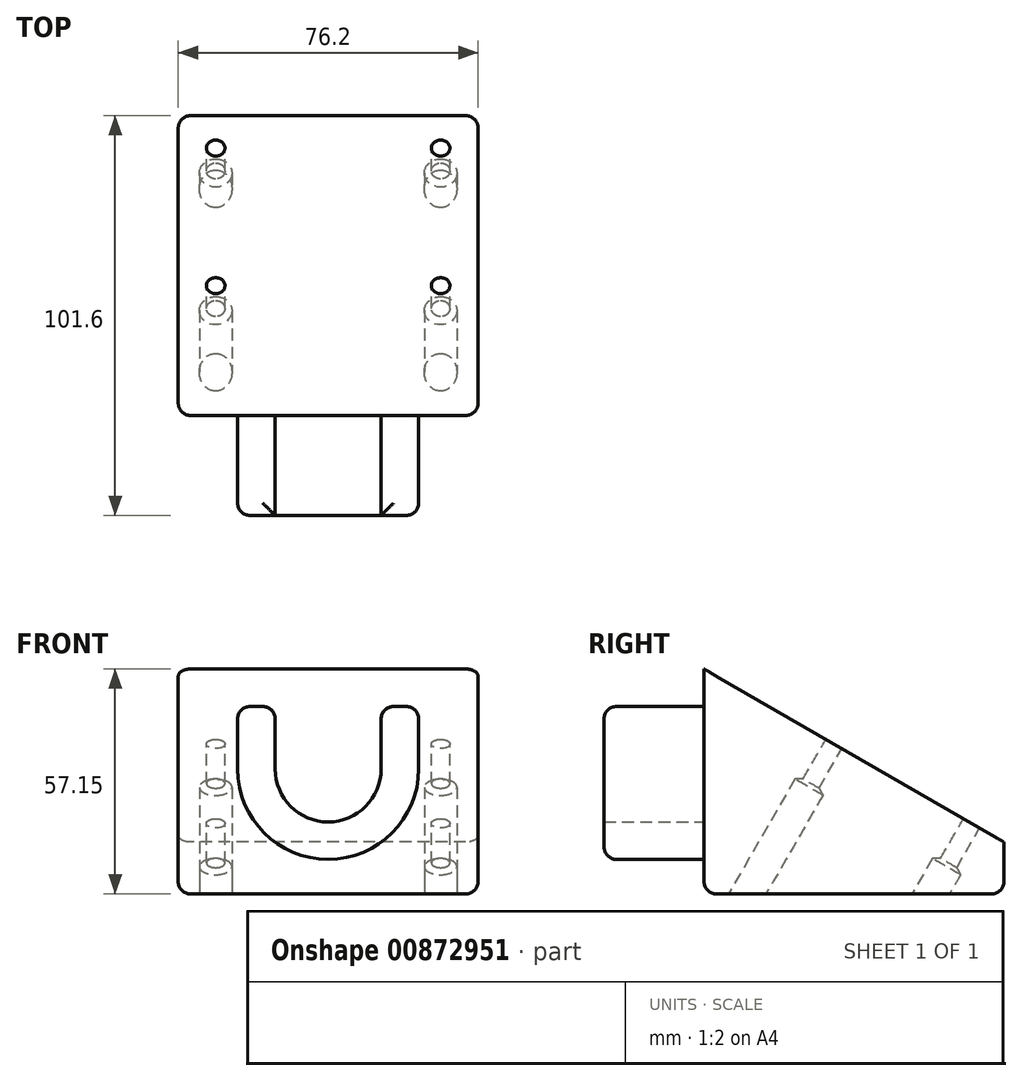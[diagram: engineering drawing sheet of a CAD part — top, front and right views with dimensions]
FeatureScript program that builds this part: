
annotation { "Feature Type Name" : "Feature", "Feature Type Description" : "" }
export const myFeature = defineFeature(function(context is Context, id is Id, definition is map)
    precondition{}
    {
        {
            var Q0;
            Q0=qCreatedBy(makeId("Right.planeOp"),FACE);
            var sketch = newSketch(context, id + "F0", { "sketchPlane" : qUnion([Q0])});
            skLineSegment(sketch, "E0", {"start": v(-38.1, -25.4) * mm, "end": v(-38.1, 31.75) * mm});
            skLineSegment(sketch, "E1", {"start": v(-38.1, 31.75) * mm, "end": v(38.1, -12.24) * mm});
            skLineSegment(sketch, "E2", {"start": v(38.1, -12.24) * mm, "end": v(38.1, -25.4) * mm});
            skLineSegment(sketch, "E3", {"start": v(38.1, -25.4) * mm, "end": v(-38.1, -25.4) * mm});
            skSolve(sketch);
        }
        {
            var Q0;
            Q0 = qSketchRegion(id + "F0", true);
            extrude(context, id + "F1", {"entities" : qUnion([Q0]), "endBound" : BoundingType.SYMMETRIC, "depth" : 76.2 * mm, "offsetDistance" : 25.4 * mm});
        }
        {
            var Q0;
            Q0=makeQuery(id+"F1.opExtrude","SWEPT_FACE",FACE,{"disambiguationData":[OSD([sQuery(id+"F0.wireOp",EDGE,"E1")])]});
            var sketch = newSketch(context, id + "F2", { "sketchPlane" : qUnion([Q0])});
            skPoint(sketch, "E4", {"position": v(28.58, -10.77) * mm});
            skPoint(sketch, "E5", {"position": v(-28.58, -10.77) * mm});
            skPoint(sketch, "E6", {"position": v(-28.58, 29.6) * mm});
            skPoint(sketch, "E7", {"position": v(28.58, 29.6) * mm});
            skSolve(sketch);
        }
        {
            var Q0;
            Q0=sQuery(id+"F2.wireOp",VERTEX,"E4");
            var Q1;
            Q1=sQuery(id+"F2.wireOp",VERTEX,"E5");
            var Q2;
            Q2=sQuery(id+"F2.wireOp",VERTEX,"E6");
            var Q3;
            Q3=sQuery(id+"F2.wireOp",VERTEX,"E7");
            var Q4;
            Q4=makeQuery(id+"F1.opExtrude","SWEPT_BODY",BODY,{"disambiguationData":[OSD([sQuery(id+"F0.wireOp",EDGE,"E0"),sQuery(id+"F0.wireOp",EDGE,"E1"),sQuery(id+"F0.wireOp",EDGE,"E2"),sQuery(id+"F0.wireOp",EDGE,"E3")])]});
            hole(context, id + "F3", {"style" : HoleStyle.SIMPLE, "endStyle" : HoleEndStyle.THROUGH, "holeDiameter" : 4.7 * mm, "majorDiameter" : 6.35 * mm, "isTappedThrough" : true, "tappedDepth" : 12.7 * mm, "tapClearance" : 3, "startFromSketch" : true, "locations" : qUnion([Q0, Q1, Q2, Q3]), "scope" : qUnion([Q4])});
        }
        {
            var Q0;
            Q0=makeQuery(id+"F1.opExtrude","SWEPT_FACE",FACE,{"disambiguationData":[OSD([sQuery(id+"F0.wireOp",EDGE,"E1")])]});
            cPlane(context, id + "F4", {"entities" : qUnion([Q0]), "cplaneType" : CPlaneType.OFFSET, "offset" : 50.8 * mm, "oppositeDirection" : true, "width" : 152.4 * mm, "height" : 152.4 * mm});
        }
        {
            var Q0;
            Q0=makeQuery(id+"F1.opExtrude","CAP_EDGE",EDGE,{"disambiguationData":[OSD([sQuery(id+"F0.wireOp",EDGE,"E0")])],"isStart":true});
            var Q1;
            Q1=makeQuery(id+"F1.opExtrude","SWEPT_EDGE",EDGE,{"disambiguationData":[OSD([sQuery(id+"F0.wireOp",EDGE,"E0"),sQuery(id+"F0.wireOp",EDGE,"E3")])]});
            var Q2;
            Q2=makeQuery(id+"F1.opExtrude","CAP_EDGE",EDGE,{"disambiguationData":[OSD([sQuery(id+"F0.wireOp",EDGE,"E0")])],"isStart":false});
            var Q3;
            Q3=makeQuery(id+"Fq0WBYdLr7NSi5U_1.opExtrude","CAP_EDGE",EDGE,{"disambiguationData":[OSD([sQuery(id+"FrXtJaCBtCV5GGo_1.wireOp",EDGE,"9FGkQ3LB-HThc-SIEn-fgRf-7n9HdzjLQJnk")])],"isStart":false});
            var Q4;
            Q4=makeQuery(id+"Fq0WBYdLr7NSi5U_1.opExtrude","SWEPT_EDGE",EDGE,{"disambiguationData":[OSD([sQuery(id+"FrXtJaCBtCV5GGo_1.wireOp",EDGE,"kfm12o6b-Ygkv-3gQt-pRsF-2uML4Z3GkxZj"),sQuery(id+"FrXtJaCBtCV5GGo_1.wireOp",EDGE,"72mObI0o-LXqr-jQ3M-gikS-OxeNh4zNZLR7")])]});
            var Q5;
            Q5=makeQuery(id+"Fq0WBYdLr7NSi5U_1.opExtrude","SWEPT_EDGE",EDGE,{"disambiguationData":[OSD([sQuery(id+"FrXtJaCBtCV5GGo_1.wireOp",EDGE,"72mObI0o-LXqr-jQ3M-gikS-OxeNh4zNZLR7"),sQuery(id+"FrXtJaCBtCV5GGo_1.wireOp",EDGE,"V3GHElQX-yl3N-O8Xa-FULM-PD9tNj9OHj6n")])]});
            var Q6;
            Q6=makeQuery(id+"Fq0WBYdLr7NSi5U_1.opExtrude","CAP_EDGE",EDGE,{"disambiguationData":[OSD([sQuery(id+"FrXtJaCBtCV5GGo_1.wireOp",EDGE,"72mObI0o-LXqr-jQ3M-gikS-OxeNh4zNZLR7")])],"isStart":false});
            var Q7;
            Q7=makeQuery(id+"Fq0WBYdLr7NSi5U_1.opExtrude","SWEPT_EDGE",EDGE,{"disambiguationData":[OSD([sQuery(id+"FrXtJaCBtCV5GGo_1.wireOp",EDGE,"rJjmnsCy-hfQL-dyx3-TJuk-Zki0aLkVcdCa"),sQuery(id+"FrXtJaCBtCV5GGo_1.wireOp",EDGE,"PnHGQfHW-PF6i-Ffau-Pvld-3sTg5STUGa7t")])]});
            var Q8;
            Q8=makeQuery(id+"Fq0WBYdLr7NSi5U_1.opExtrude","SWEPT_EDGE",EDGE,{"disambiguationData":[OSD([sQuery(id+"FrXtJaCBtCV5GGo_1.wireOp",EDGE,"KI4g5WDN-T7LZ-MRyy-Vtqw-rKYS9IoMxQUQ"),sQuery(id+"FrXtJaCBtCV5GGo_1.wireOp",EDGE,"rJjmnsCy-hfQL-dyx3-TJuk-Zki0aLkVcdCa")])]});
            var Q9;
            Q9=makeQuery(id+"Fq0WBYdLr7NSi5U_1.opExtrude","CAP_EDGE",EDGE,{"disambiguationData":[OSD([sQuery(id+"FrXtJaCBtCV5GGo_1.wireOp",EDGE,"rJjmnsCy-hfQL-dyx3-TJuk-Zki0aLkVcdCa")])],"isStart":false});
            var Q10;
            Q10=makeQuery(id+"F1.opExtrude","CAP_EDGE",EDGE,{"disambiguationData":[OSD([sQuery(id+"F0.wireOp",EDGE,"E3")])],"isStart":true});
            var Q11;
            Q11=makeQuery(id+"F1.opExtrude","CAP_EDGE",EDGE,{"disambiguationData":[OSD([sQuery(id+"F0.wireOp",EDGE,"E3")])],"isStart":false});
            var Q12;
            Q12=makeQuery(id+"F1.opExtrude","SWEPT_EDGE",EDGE,{"disambiguationData":[OSD([sQuery(id+"F0.wireOp",EDGE,"E2"),sQuery(id+"F0.wireOp",EDGE,"E3")])]});
            var Q13;
            Q13=makeQuery(id+"F1.opExtrude","CAP_EDGE",EDGE,{"disambiguationData":[OSD([sQuery(id+"F0.wireOp",EDGE,"E2")])],"isStart":false});
            var Q14;
            Q14=makeQuery(id+"F1.opExtrude","CAP_EDGE",EDGE,{"disambiguationData":[OSD([sQuery(id+"F0.wireOp",EDGE,"E2")])],"isStart":true});
            fillet(context, id + "F5", {"entities" : qUnion([Q0, Q1, Q2, Q3, Q4, Q5, Q6, Q7, Q8, Q9, Q10, Q11, Q12, Q13, Q14]), "radius" : 3.17 * mm, "tangentPropagation" : true, "allowEdgeOverflow" : false});
        }
        {
            var Q0;
            Q0=qCreatedBy(id+"F4.planeOp",FACE);
            var sketch = newSketch(context, id + "F6", { "sketchPlane" : qUnion([Q0])});
            skCircle(sketch, "E8.0", {"center": v(28.58, -10.77) * mm, "radius": 2.35 * mm});
            skCircle(sketch, "E8.1", {"center": v(28.58, 29.6) * mm, "radius": 2.35 * mm});
            skCircle(sketch, "E8.2", {"center": v(-28.58, 29.6) * mm, "radius": 2.35 * mm});
            skCircle(sketch, "E8.3", {"center": v(-28.58, -10.77) * mm, "radius": 2.35 * mm});
            skSolve(sketch);
        }
        {
            var Q0;
            Q0=sQuery(id+"F6.wireOp",VERTEX,"E8.3.center");
            var Q1;
            Q1=sQuery(id+"F6.wireOp",VERTEX,"E8.0.center");
            var Q2;
            Q2=sQuery(id+"F6.wireOp",VERTEX,"E8.1.center");
            var Q3;
            Q3=sQuery(id+"F6.wireOp",VERTEX,"E8.2.center");
            var Q4;
            Q4=makeQuery(id+"F1.opExtrude","SWEPT_BODY",BODY,{"disambiguationData":[OSD([sQuery(id+"F0.wireOp",EDGE,"E0"),sQuery(id+"F0.wireOp",EDGE,"E1"),sQuery(id+"F0.wireOp",EDGE,"E2"),sQuery(id+"F0.wireOp",EDGE,"E3")])]});
            hole(context, id + "F7", {"style" : HoleStyle.SIMPLE, "endStyle" : HoleEndStyle.BLIND, "oppositeDirection" : true, "holeDiameter" : 8.25 * mm, "majorDiameter" : 6.35 * mm, "holeDepth" : 38.1 * mm, "isTappedThrough" : true, "tappedDepth" : 12.7 * mm, "tapClearance" : 3, "startFromSketch" : true, "locations" : qUnion([Q0, Q1, Q2, Q3]), "scope" : qUnion([Q4])});
        }
        {
            var Q0;
            Q0=makeQuery(id+"F1.opExtrude","SWEPT_FACE",FACE,{"disambiguationData":[OSD([sQuery(id+"F0.wireOp",EDGE,"E0")])]});
            var sketch = newSketch(context, id + "F8", { "sketchPlane" : qUnion([Q0])});
            skPoint(sketch, "E9", {"position": v(0, 6.35) * mm});
            skArc(sketch, "E10", {"start": v(-13.46, 6.35) * mm, "mid": v(0, -7.11) * mm, "end": v(13.46, 6.35) * mm});
            skArc(sketch, "E11", {"start": v(-22.99, 6.35) * mm, "mid": v(0, -16.64) * mm, "end": v(22.99, 6.35) * mm});
            skLineSegment(sketch, "E12", {"start": v(-55.53, 6.35) * mm, "end": v(61.34, 6.35) * mm, "construction": true});
            skLineSegment(sketch, "E13", {"start": v(-22.99, 6.35) * mm, "end": v(-22.99, 22.22) * mm});
            skLineSegment(sketch, "E14", {"start": v(-13.46, 22.22) * mm, "end": v(-22.99, 22.22) * mm});
            skLineSegment(sketch, "E15", {"start": v(-13.46, 6.35) * mm, "end": v(-13.46, 22.22) * mm});
            skLineSegment(sketch, "E16", {"start": v(13.46, 6.35) * mm, "end": v(13.46, 22.22) * mm});
            skLineSegment(sketch, "E17", {"start": v(22.99, 22.22) * mm, "end": v(22.99, 6.35) * mm});
            skLineSegment(sketch, "E18", {"start": v(22.99, 22.22) * mm, "end": v(13.46, 22.22) * mm});
            skSolve(sketch);
        }
        {
            var Q0;
            Q0=makeQuery(id+"F8.imprint","IMPRINT",FACE,{"disambiguationData":[TD([[makeQuery(id+"F8.imprint","IMPRINT",EDGE,{"derivedFrom":sQuery(id+"F8.wireOp",EDGE,"E10")}),-1.0]])]});
            extrude(context, id + "F9", {"entities" : qUnion([Q0]), "operationType" : NewBodyOperationType.ADD, "depth" : 25.4 * mm, "offsetDistance" : 25.4 * mm});
        }
        {
            var Q0;
            Q0=makeQuery(id+"F9.opExtrude","CAP_EDGE",EDGE,{"disambiguationData":[OSD([sQuery(id+"F8.wireOp",EDGE,"E11")])],"isStart":true});
            var Q1;
            Q1=makeQuery(id+"F9.opExtrude","CAP_EDGE",EDGE,{"disambiguationData":[OSD([sQuery(id+"F8.wireOp",EDGE,"E11")])],"isStart":false});
            var Q2;
            Q2=makeQuery(id+"F9.opExtrude","CAP_EDGE",EDGE,{"disambiguationData":[OSD([sQuery(id+"F8.wireOp",EDGE,"E14")])],"isStart":true});
            var Q3;
            Q3=makeQuery(id+"F9.opExtrude","CAP_EDGE",EDGE,{"disambiguationData":[OSD([sQuery(id+"F8.wireOp",EDGE,"E18")])],"isStart":true});
            var Q4;
            Q4=makeQuery(id+"F9.opExtrude","SWEPT_EDGE",EDGE,{"disambiguationData":[OSD([sQuery(id+"F8.wireOp",EDGE,"E13"),sQuery(id+"F8.wireOp",EDGE,"E14")])]});
            var Q5;
            Q5=makeQuery(id+"F9.opExtrude","SWEPT_EDGE",EDGE,{"disambiguationData":[OSD([sQuery(id+"F8.wireOp",EDGE,"E14"),sQuery(id+"F8.wireOp",EDGE,"E15")])]});
            var Q6;
            Q6=makeQuery(id+"F9.opExtrude","SWEPT_EDGE",EDGE,{"disambiguationData":[OSD([sQuery(id+"F8.wireOp",EDGE,"E16"),sQuery(id+"F8.wireOp",EDGE,"E18")])]});
            var Q7;
            Q7=makeQuery(id+"F9.opExtrude","CAP_EDGE",EDGE,{"disambiguationData":[OSD([sQuery(id+"F8.wireOp",EDGE,"E14")])],"isStart":false});
            var Q8;
            Q8=makeQuery(id+"F9.opExtrude","CAP_EDGE",EDGE,{"disambiguationData":[OSD([sQuery(id+"F8.wireOp",EDGE,"E18")])],"isStart":false});
            var Q9;
            Q9=makeQuery(id+"F9.opExtrude","SWEPT_EDGE",EDGE,{"disambiguationData":[OSD([sQuery(id+"F8.wireOp",EDGE,"E17"),sQuery(id+"F8.wireOp",EDGE,"E18")])]});
            fillet(context, id + "F10", {"entities" : qUnion([Q0, Q1, Q2, Q3, Q4, Q5, Q6, Q7, Q8, Q9]), "radius" : 3.17 * mm, "tangentPropagation" : true, "allowEdgeOverflow" : false});
        }
    });
